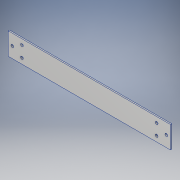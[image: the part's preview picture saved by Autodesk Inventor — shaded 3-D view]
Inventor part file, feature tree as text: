
AUTODESK INVENTOR PART (.ipt)
format: ipt  version: 2017 (Build 210142000, 142)  size: 109,568 bytes
history: native  units: in
note: dims shown in document units (in); Inventor stores cm internally (conversion verified against a paired STEP export)
features: extrude x1
ambient origin geometry x8: Origin, YZ Plane, XZ Plane, XY Plane, X Axis, Y Axis, Z Axis, Center Point
bodies: Body1 (feature_tree)
feature tree (1):
  extrude  "Extrusion2"  Depth=14.75in
